# Revit family: EKF_EE_ЗадняяПанельTrivia_AVERES
name_source: partatom
category: Электрооборудование
units: mm (PartAtom-declared; Revit-internal decimal feet)

## family parameters
Всегда вертикально = Нет
На основе рабочей плоскости = Да
Общий = Да
При загрузке вырезать с полостями = Нет
Размер круглого соединителя = Использовать диаметр
Тип детали = Силовой щит
Точка расчета площади = Нет

## types (8) — shared parameters
ADSK_Единица измерения = шт.
ADSK_Завод-изготовитель = EKF
ADSK_Количество = 1
ADSK_Марка = Задняя панель
ADSK_Материал = RAL 7035_Сталь
ADSK_Обозначение = Задняя панель
ADSK_Размер_Высота = 2003 мм
ADSK_Размер_Глубина = 20 мм
Изготовитель = EKF
Отметка по умолчанию = 1219.2 мм
Серия номенклатуры = Averes
ТВ = EKF_2_TRIVIA_AVERES
Тип установки = -
zero-valued in all types: ADSK_Масса

## per-type parameters (varying)
| type | ADSK_Код изделия | ADSK_Размер_Ширина | IP55 | Степень защиты IP | Тип |
| Задняя панель Ш300 IP30 EKF AVERES | PR300 | 309 мм | Нет | IP30 | 449 мм |
| Задняя панель Ш300 IP55 EKF AVERES | PR300WP | 309 мм | Нет | IP55 | 450 мм |
| Задняя панель Ш400 IP30 EKF AVERES | PR400 | 409 мм | Да | IP30 | 451 мм |
| Задняя панель Ш400 IP55 EKF AVERES | PR400WP | 409 мм | Нет | IP55 | 452 мм |
| Задняя панель Ш600 IP30 EKF AVERES | PR600 | 609 мм | Да | IP30 | 453 мм |
| Задняя панель Ш600 IP55 EKF AVERES | PR600WP | 609 мм | Нет | IP55 | 454 мм |
| Задняя панель Ш800 IP30 EKF AVERES | PR800 | 809 мм | Да | IP30 | 455 мм |
| Задняя панель Ш800 IP55 EKF AVERES | PR800WP | 809 мм | Нет | IP55 | 456 мм |

note: column(s) folded — value = type name in every type: ADSK_Наименование
